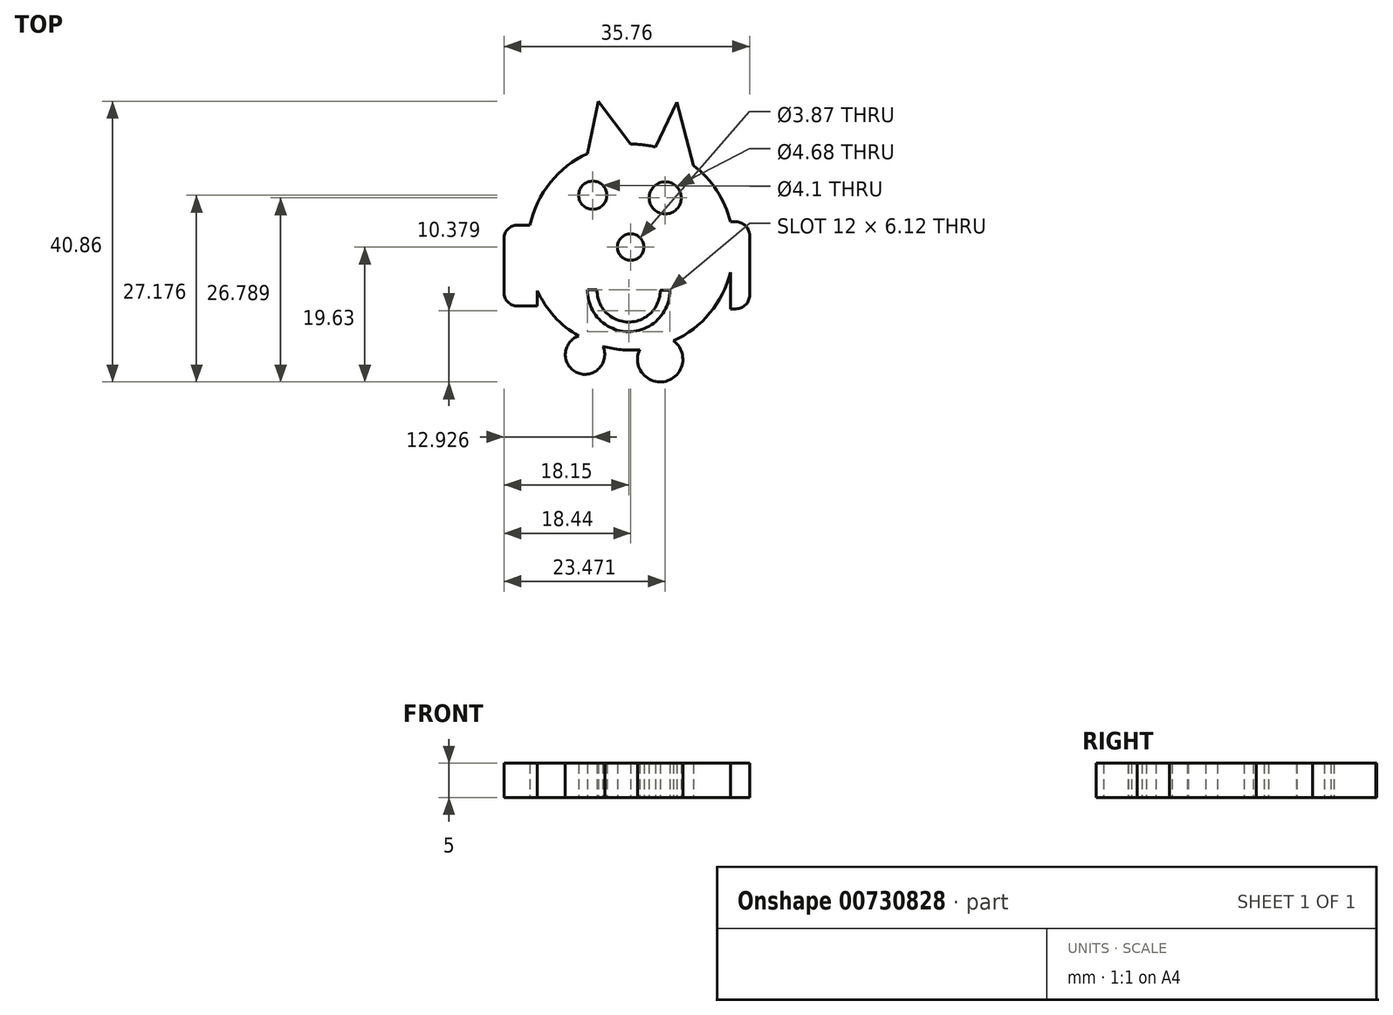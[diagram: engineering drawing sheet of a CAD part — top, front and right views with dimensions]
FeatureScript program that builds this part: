
annotation { "Feature Type Name" : "Feature", "Feature Type Description" : "" }
export const myFeature = defineFeature(function(context is Context, id is Id, definition is map)
    precondition{}
    {
        {
            var Q0;
            Q0=qCreatedBy(makeId("Top.planeOp"),FACE);
            var sketch = newSketch(context, id + "F0", { "sketchPlane" : qUnion([Q0])});
            skCircle(sketch, "E0", {"center": v(0, 0) * mm, "radius": 15 * mm});
            skLineSegment(sketch, "E1", {"start": v(-6.31, 13.6) * mm, "end": v(-4.68, 21.23) * mm});
            skLineSegment(sketch, "E2", {"start": v(-4.68, 21.23) * mm, "end": v(0, 15) * mm});
            skLineSegment(sketch, "E3", {"start": v(3.6, 14.56) * mm, "end": v(6.73, 21.08) * mm});
            skLineSegment(sketch, "E4", {"start": v(6.73, 21.08) * mm, "end": v(9.12, 11.91) * mm});
            skCircle(sketch, "E5", {"center": v(-5.51, 7.55) * mm, "radius": 2.05 * mm});
            skCircle(sketch, "E6", {"center": v(5.03, 7.16) * mm, "radius": 2.34 * mm});
            skCircle(sketch, "E7", {"center": v(0, 0) * mm, "radius": 1.93 * mm});
            skArc(sketch, "E8", {"start": v(-6.29, -6.2) * mm, "mid": v(-0.34, -12.3) * mm, "end": v(5.7, -6.29) * mm});
            skArc(sketch, "E9.0", {"start": v(-4.89, -6.22) * mm, "mid": v(-0.33, -10.9) * mm, "end": v(4.3, -6.3) * mm});
            skLineSegment(sketch, "E10", {"start": v(-6.29, -6.2) * mm, "end": v(-4.89, -6.22) * mm});
            skLineSegment(sketch, "E11", {"start": v(4.3, -6.3) * mm, "end": v(5.7, -6.29) * mm});
            skLineSegment(sketch, "E12.bottom", {"start": v(-16.44, 3.21) * mm, "end": v(-13.6, 3.21) * mm});
            skLineSegment(sketch, "E12.top", {"start": v(-16.44, -8.6) * mm, "end": v(-13.6, -8.6) * mm});
            skLineSegment(sketch, "E12.left", {"start": v(-18.44, 1.21) * mm, "end": v(-18.44, -6.6) * mm});
            skLineSegment(sketch, "E12.right", {"start": v(-13.6, 3.21) * mm, "end": v(-13.6, -8.6) * mm});
            skLineSegment(sketch, "E13.bottom", {"start": v(14.54, 3.67) * mm, "end": v(15.32, 3.67) * mm});
            skLineSegment(sketch, "E13.top", {"start": v(14.54, -8.98) * mm, "end": v(15.32, -8.98) * mm});
            skLineSegment(sketch, "E13.left", {"start": v(14.54, 3.67) * mm, "end": v(14.54, -8.98) * mm});
            skLineSegment(sketch, "E13.right", {"start": v(17.32, 1.67) * mm, "end": v(17.32, -6.98) * mm});
            skCircle(sketch, "E14", {"center": v(-6.64, -15.65) * mm, "radius": 2.87 * mm});
            skCircle(sketch, "E15", {"center": v(4.3, -16.33) * mm, "radius": 3.3 * mm});
            skPoint(sketch, "E16.visualSharp", {"position": v(17.32, -8.98) * mm});
            skArc(sketch, "E16.filletArc", {"start": v(15.32, -8.98) * mm, "mid": v(16.74, -8.4) * mm, "end": v(17.32, -6.98) * mm});
            skPoint(sketch, "E17.visualSharp", {"position": v(17.32, 3.67) * mm});
            skArc(sketch, "E17.filletArc", {"start": v(17.32, 1.67) * mm, "mid": v(16.74, 3.09) * mm, "end": v(15.32, 3.67) * mm});
            skPoint(sketch, "E18.visualSharp", {"position": v(-18.44, 3.21) * mm});
            skArc(sketch, "E18.filletArc", {"start": v(-16.44, 3.21) * mm, "mid": v(-17.85, 2.63) * mm, "end": v(-18.44, 1.21) * mm});
            skPoint(sketch, "E19.visualSharp", {"position": v(-18.44, -8.6) * mm});
            skArc(sketch, "E19.filletArc", {"start": v(-18.44, -6.6) * mm, "mid": v(-17.85, -8) * mm, "end": v(-16.44, -8.6) * mm});
            skSolve(sketch);
        }
        {
            var Q0;
            Q0=makeQuery(id+"F0.imprint","IMPRINT",FACE,{"disambiguationData":[TD([[makeQuery(id+"F0.imprint","IMPRINT",EDGE,{"derivedFrom":sQuery(id+"F0.wireOp",EDGE,"E5")}),-1.0]])]});
            var Q1;
            {var subQ0=sQuery(id+"F0.wireOp",EDGE,"E15");var subQ1=sQuery(id+"F0.wireOp",EDGE,"E0");var subQ2=makeQuery(id+"F0.imprint","INTERSECT",VERTEX,{"disambiguationData":[OD(0.0)],"derivedFrom":[subQ1,subQ0]});Q1=makeQuery(id+"F0.imprint","IMPRINT",FACE,{"disambiguationData":[TD([[makeQuery(id+"F0.imprint","IMPRINT",EDGE,{"disambiguationData":[TD([[subQ2,-1.0]])],"derivedFrom":subQ1}),1.0]])]});}
            var Q2;
            {var subQ0=sQuery(id+"F0.wireOp",EDGE,"E15");var subQ1=sQuery(id+"F0.wireOp",EDGE,"E0");var subQ2=makeQuery(id+"F0.imprint","INTERSECT",VERTEX,{"disambiguationData":[OD(0.0)],"derivedFrom":[subQ1,subQ0]});Q2=makeQuery(id+"F0.imprint","IMPRINT",FACE,{"disambiguationData":[TD([[makeQuery(id+"F0.imprint","IMPRINT",EDGE,{"disambiguationData":[TD([[subQ2,-1.0]])],"derivedFrom":subQ1}),-1.0]])]});}
            var Q3;
            {var subQ0=sQuery(id+"F0.wireOp",EDGE,"E14");var subQ1=sQuery(id+"F0.wireOp",EDGE,"E0");var subQ2=makeQuery(id+"F0.imprint","INTERSECT",VERTEX,{"disambiguationData":[OD(0.0)],"derivedFrom":[subQ1,subQ0]});Q3=makeQuery(id+"F0.imprint","IMPRINT",FACE,{"disambiguationData":[TD([[makeQuery(id+"F0.imprint","IMPRINT",EDGE,{"disambiguationData":[TD([[subQ2,-1.0]])],"derivedFrom":subQ1}),-1.0]])]});}
            var Q4;
            {var subQ0=sQuery(id+"F0.wireOp",EDGE,"E14");var subQ1=sQuery(id+"F0.wireOp",EDGE,"E0");var subQ2=makeQuery(id+"F0.imprint","INTERSECT",VERTEX,{"disambiguationData":[OD(0.0)],"derivedFrom":[subQ1,subQ0]});Q4=makeQuery(id+"F0.imprint","IMPRINT",FACE,{"disambiguationData":[TD([[makeQuery(id+"F0.imprint","IMPRINT",EDGE,{"disambiguationData":[TD([[subQ2,-1.0]])],"derivedFrom":subQ1}),1.0]])]});}
            var Q5;
            {var subQ4=sQuery(id+"F0.wireOp",EDGE,"E13.bottom");Q5=makeQuery(id+"F0.imprint","IMPRINT",FACE,{"disambiguationData":[TD([[makeQuery(id+"F0.imprint","IMPRINT",EDGE,{"derivedFrom":subQ4}),-1.0]])]});}
            var Q6;
            {var subQ0=sQuery(id+"F0.wireOp",EDGE,"E13.left");var subQ1=sQuery(id+"F0.wireOp",EDGE,"E0");var subQ3=makeQuery(id+"F0.imprint","INTERSECT",VERTEX,{"derivedFrom":[subQ1,subQ0]});Q6=makeQuery(id+"F0.imprint","IMPRINT",FACE,{"disambiguationData":[TD([[makeQuery(id+"F0.imprint","IMPRINT",EDGE,{"disambiguationData":[TD([[subQ3,-1.0]])],"derivedFrom":subQ1}),1.0]])]});}
            var Q7;
            {var subQ4=sQuery(id+"F0.wireOp",EDGE,"E12.top");Q7=makeQuery(id+"F0.imprint","IMPRINT",FACE,{"disambiguationData":[TD([[makeQuery(id+"F0.imprint","IMPRINT",EDGE,{"derivedFrom":subQ4}),1.0]])]});}
            var Q8;
            {var subQ0=sQuery(id+"F0.wireOp",EDGE,"E12.bottom");var subQ1=sQuery(id+"F0.wireOp",EDGE,"E0");var subQ2=makeQuery(id+"F0.imprint","INTERSECT",VERTEX,{"derivedFrom":[subQ1,subQ0]});Q8=makeQuery(id+"F0.imprint","IMPRINT",FACE,{"disambiguationData":[TD([[makeQuery(id+"F0.imprint","IMPRINT",EDGE,{"disambiguationData":[TD([[subQ2,-1.0]])],"derivedFrom":subQ1}),1.0]])]});}
            var Q9;
            {var subQ0=sQuery(id+"F0.wireOp",EDGE,"E1");Q9=makeQuery(id+"F0.imprint","IMPRINT",FACE,{"disambiguationData":[TD([[makeQuery(id+"F0.imprint","IMPRINT",EDGE,{"derivedFrom":subQ0}),-1.0]])]});}
            var Q10;
            {var subQ0=sQuery(id+"F0.wireOp",EDGE,"E3");Q10=makeQuery(id+"F0.imprint","IMPRINT",FACE,{"disambiguationData":[TD([[makeQuery(id+"F0.imprint","IMPRINT",EDGE,{"derivedFrom":subQ0}),-1.0]])]});}
            extrude(context, id + "F1", {"entities" : qUnion([Q0, Q1, Q2, Q3, Q4, Q5, Q6, Q7, Q8, Q9, Q10]), "depth" : 5 * mm, "offsetDistance" : 25 * mm});
        }
    });
